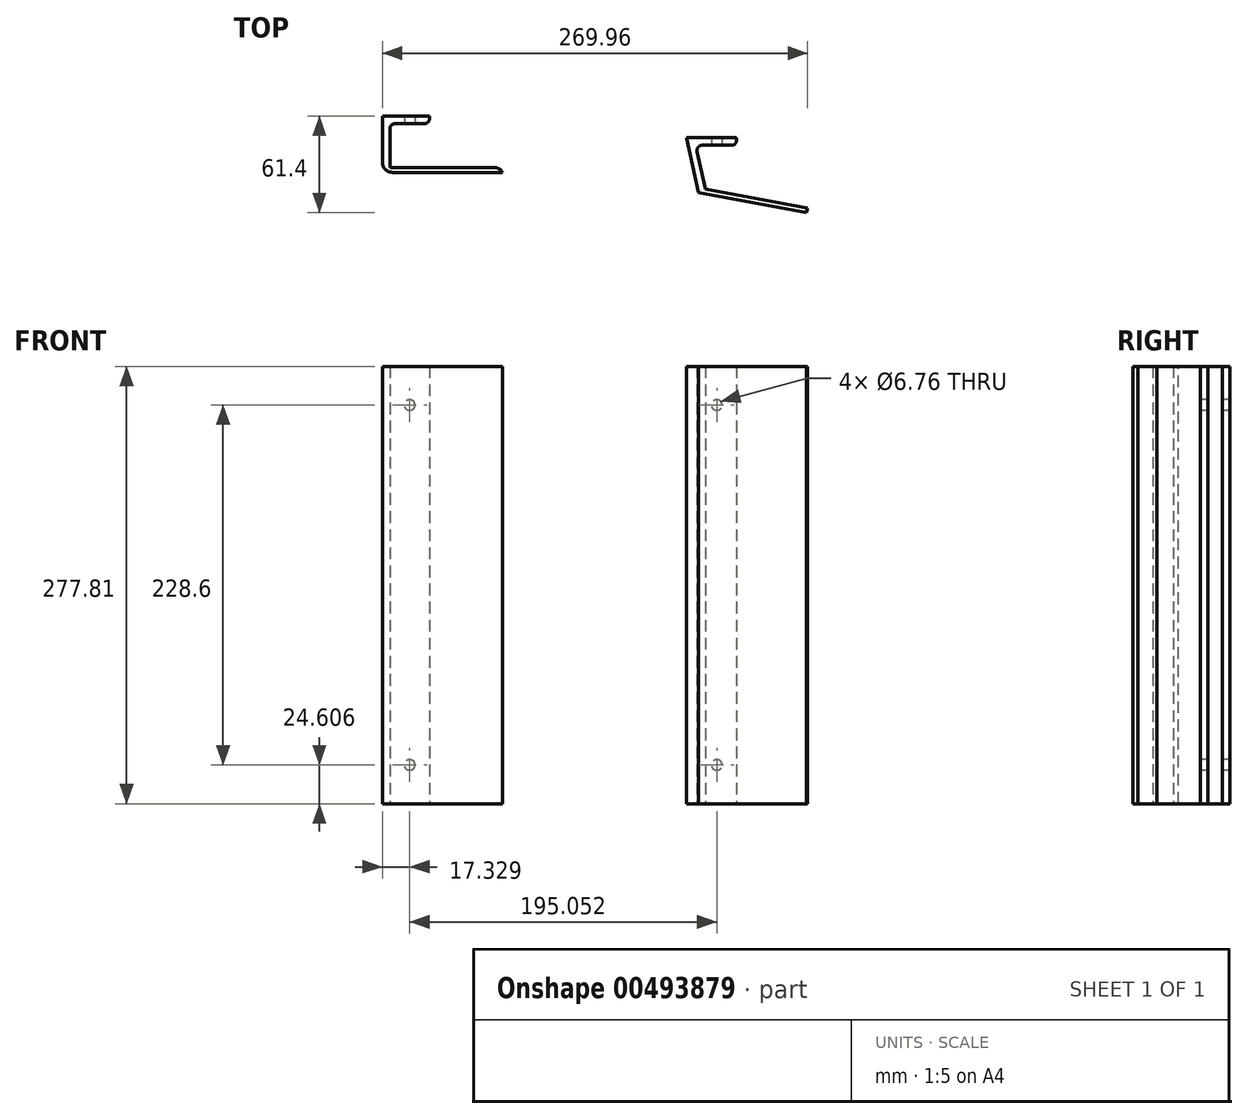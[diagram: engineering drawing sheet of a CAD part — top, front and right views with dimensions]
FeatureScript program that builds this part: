
annotation { "Feature Type Name" : "Feature", "Feature Type Description" : "" }
export const myFeature = defineFeature(function(context is Context, id is Id, definition is map)
    precondition{}
    {
        {
            var Q0;
            Q0=qCreatedBy(makeId("Top.planeOp"),FACE);
            var sketch = newSketch(context, id + "F0", { "sketchPlane" : qUnion([Q0])});
            skLineSegment(sketch, "E0", {"start": v(0, 0) * mm, "end": v(-31.75, 0) * mm});
            skLineSegment(sketch, "E1", {"start": v(-31.75, 0) * mm, "end": v(-24.24, -34.92) * mm});
            skLineSegment(sketch, "E2", {"start": v(-24.24, -34.92) * mm, "end": v(44.45, -47.63) * mm});
            skLineSegment(sketch, "E3", {"start": v(44.45, -47.63) * mm, "end": v(45.03, -44.5) * mm});
            skLineSegment(sketch, "E4", {"start": v(0, 0) * mm, "end": v(0, -1.59) * mm});
            skLineSegment(sketch, "E5", {"start": v(-3.18, -4.76) * mm, "end": v(-21.92, -4.76) * mm});
            skLineSegment(sketch, "E6", {"start": v(-25.03, -8.6) * mm, "end": v(-19.89, -32.5) * mm});
            skLineSegment(sketch, "E7", {"start": v(-19.89, -32.5) * mm, "end": v(45.03, -44.5) * mm});
            skPoint(sketch, "E8.visualSharp", {"position": v(-25.85, -4.76) * mm});
            skArc(sketch, "E8.filletArc", {"start": v(-21.92, -4.76) * mm, "mid": v(-24.4, -5.94) * mm, "end": v(-25.03, -8.6) * mm});
            skPoint(sketch, "E9.visualSharp", {"position": v(0, -4.76) * mm});
            skArc(sketch, "E9.filletArc", {"start": v(-3.18, -4.76) * mm, "mid": v(-0.93, -3.83) * mm, "end": v(0, -1.59) * mm});
            skSolve(sketch);
        }
        {
            var Q0;
            Q0=makeQuery(id+"F0.imprint","IMPRINT",FACE,{"disambiguationData":[TD([[makeQuery(id+"F0.imprint","IMPRINT",EDGE,{"derivedFrom":sQuery(id+"F0.wireOp",EDGE,"E0")}),1.0]])]});
            extrude(context, id + "F1", {"entities" : qUnion([Q0]), "depth" : 277.8 * mm});
        }
        {
            var Q0;
            Q0=makeQuery(id+"F1.opExtrude","SWEPT_FACE",FACE,{"disambiguationData":[OSD([sQuery(id+"F0.wireOp",EDGE,"E5")])]});
            var sketch = newSketch(context, id + "F2", { "sketchPlane" : qUnion([Q0])});
            skLineSegment(sketch, "E10", {"start": v(-12.55, 24.6) * mm, "end": v(-12.55, 253.2) * mm, "construction": true});
            skPoint(sketch, "E10.startSnap0", {"position": v(-12.55, 0) * mm});
            skPoint(sketch, "E10.endSnap0", {"position": v(-12.55, 277.81) * mm});
            skLineSegment(sketch, "E11", {"start": v(-21.92, 138.9) * mm, "end": v(-3.18, 138.9) * mm, "construction": true});
            skPoint(sketch, "E12", {"position": v(-12.55, 138.9) * mm});
            skSolve(sketch);
        }
        {
            var Q0;
            Q0=sQuery(id+"F2.wireOp",VERTEX,"E10.end");
            var Q1;
            Q1=sQuery(id+"F2.wireOp",VERTEX,"E10.start");
            var Q2;
            Q2=makeQuery(id+"F1.opExtrude","SWEPT_BODY",BODY,{"disambiguationData":[OSD([sQuery(id+"F0.wireOp",EDGE,"E0"),sQuery(id+"F0.wireOp",EDGE,"E1"),sQuery(id+"F0.wireOp",EDGE,"E2"),sQuery(id+"F0.wireOp",EDGE,"E3"),sQuery(id+"F0.wireOp",EDGE,"E4"),sQuery(id+"F0.wireOp",EDGE,"E5"),sQuery(id+"F0.wireOp",EDGE,"E6"),sQuery(id+"F0.wireOp",EDGE,"E7"),sQuery(id+"F0.wireOp",EDGE,"E8.filletArc"),sQuery(id+"F0.wireOp",EDGE,"E9.filletArc")])]});
            hole(context, id + "F3", {"style" : HoleStyle.SIMPLE, "endStyle" : HoleEndStyle.THROUGH, "standardTappedOrClearance" : lookupTablePath({ "standard" : "ANSI", "fit" : "Normal (ASME)", "size" : "1/4", "type" : "Clearance" }), "standardBlindInLast" : lookupTablePath({ "fit" : "Free", "standard" : "ANSI", "size" : "1/4", "type" : "Clearance" }), "holeDiameter" : 6.76 * mm, "isTappedThrough" : true, "tappedDepth" : 12.7 * mm, "tapClearance" : 3, "locations" : qUnion([Q0, Q1]), "scope" : qUnion([Q2])});
        }
        {
            var Q0;
            Q0=qCreatedBy(makeId("Top.planeOp"),FACE);
            var sketch = newSketch(context, id + "F4", { "sketchPlane" : qUnion([Q0])});
            skLineSegment(sketch, "E13", {"start": v(-195.05, 13.77) * mm, "end": v(-224.93, 13.77) * mm});
            skLineSegment(sketch, "E14", {"start": v(-224.93, 13.77) * mm, "end": v(-224.93, -21.95) * mm});
            skLineSegment(sketch, "E15", {"start": v(-224.93, -21.95) * mm, "end": v(-148.73, -21.95) * mm});
            skLineSegment(sketch, "E16", {"start": v(-148.73, -21.95) * mm, "end": v(-148.73, -18.78) * mm});
            skLineSegment(sketch, "E17", {"start": v(-195.05, 13.77) * mm, "end": v(-195.05, 12.19) * mm});
            skLineSegment(sketch, "E18", {"start": v(-198.23, 9.01) * mm, "end": v(-216.98, 9.01) * mm});
            skLineSegment(sketch, "E19", {"start": v(-220.15, 5.84) * mm, "end": v(-220.15, -18.78) * mm});
            skLineSegment(sketch, "E20", {"start": v(-220.15, -18.78) * mm, "end": v(-148.73, -18.78) * mm});
            skPoint(sketch, "E21.visualSharp", {"position": v(-220.15, 9.01) * mm});
            skArc(sketch, "E21.filletArc", {"start": v(-216.98, 9.01) * mm, "mid": v(-219.22, 8.08) * mm, "end": v(-220.15, 5.84) * mm});
            skPoint(sketch, "E22.visualSharp", {"position": v(-195.05, 9.01) * mm});
            skArc(sketch, "E22.filletArc", {"start": v(-198.23, 9.01) * mm, "mid": v(-195.98, 9.94) * mm, "end": v(-195.05, 12.19) * mm});
            skSolve(sketch);
        }
        {
            var Q0;
            Q0=makeQuery(id+"F4.imprint","IMPRINT",FACE,{"disambiguationData":[TD([[makeQuery(id+"F4.imprint","IMPRINT",EDGE,{"derivedFrom":sQuery(id+"F4.wireOp",EDGE,"E13")}),1.0]])]});
            extrude(context, id + "F5", {"entities" : qUnion([Q0]), "depth" : 277.8 * mm});
        }
        {
            var Q0;
            Q0=makeQuery(id+"F5.opExtrude","SWEPT_FACE",FACE,{"disambiguationData":[OSD([sQuery(id+"F4.wireOp",EDGE,"E18")])]});
            var sketch = newSketch(context, id + "F6", { "sketchPlane" : qUnion([Q0])});
            skLineSegment(sketch, "E23", {"start": v(-207.6, 24.6) * mm, "end": v(-207.6, 253.2) * mm, "construction": true});
            skPoint(sketch, "E23.startSnap0", {"position": v(-207.6, 0) * mm});
            skPoint(sketch, "E23.endSnap0", {"position": v(-207.6, 277.81) * mm});
            skLineSegment(sketch, "E24", {"start": v(-216.98, 138.9) * mm, "end": v(-198.23, 138.9) * mm, "construction": true});
            skPoint(sketch, "E25", {"position": v(-207.6, 138.9) * mm});
            skSolve(sketch);
        }
        {
            var Q0;
            Q0=sQuery(id+"F6.wireOp",VERTEX,"E23.end");
            var Q1;
            Q1=sQuery(id+"F6.wireOp",VERTEX,"E23.start");
            var Q2;
            Q2=makeQuery(id+"F5.opExtrude","SWEPT_BODY",BODY,{"disambiguationData":[OSD([sQuery(id+"F4.wireOp",EDGE,"E13"),sQuery(id+"F4.wireOp",EDGE,"E16"),sQuery(id+"F4.wireOp",EDGE,"E17"),sQuery(id+"F4.wireOp",EDGE,"E18"),sQuery(id+"F4.wireOp",EDGE,"E19"),sQuery(id+"F4.wireOp",EDGE,"E20"),sQuery(id+"F4.wireOp",EDGE,"E21.filletArc"),sQuery(id+"F4.wireOp",EDGE,"E22.filletArc"),sQuery(id+"F4.wireOp",EDGE,"E14"),sQuery(id+"F4.wireOp",EDGE,"E15")])]});
            hole(context, id + "F7", {"style" : HoleStyle.SIMPLE, "endStyle" : HoleEndStyle.THROUGH, "standardTappedOrClearance" : lookupTablePath({ "standard" : "ANSI", "fit" : "Normal (ASME)", "size" : "1/4", "type" : "Clearance" }), "standardBlindInLast" : lookupTablePath({ "fit" : "Free", "standard" : "ANSI", "size" : "1/4", "type" : "Clearance" }), "holeDiameter" : 6.76 * mm, "isTappedThrough" : true, "tappedDepth" : 12.7 * mm, "tapClearance" : 3, "locations" : qUnion([Q0, Q1]), "scope" : qUnion([Q2])});
        }
        {
            var Q0;
            Q0=makeQuery(id+"F5.opExtrude","SWEPT_EDGE",EDGE,{"disambiguationData":[OSD([sQuery(id+"F4.wireOp",EDGE,"E14"),sQuery(id+"F4.wireOp",EDGE,"E15")])]});
            fillet(context, id + "F8", {"entities" : qUnion([Q0]), "radius" : 6.35 * mm, "tangentPropagation" : true, "allowEdgeOverflow" : false});
        }
        {
            var Q0;
            Q0=makeQuery(id+"F5.opExtrude","SWEPT_EDGE",EDGE,{"disambiguationData":[OSD([sQuery(id+"F4.wireOp",EDGE,"E16"),sQuery(id+"F4.wireOp",EDGE,"E20")])]});
            fillet(context, id + "F9", {"entities" : qUnion([Q0]), "radius" : 6.35 * mm, "tangentPropagation" : true, "allowEdgeOverflow" : false});
        }
    });
